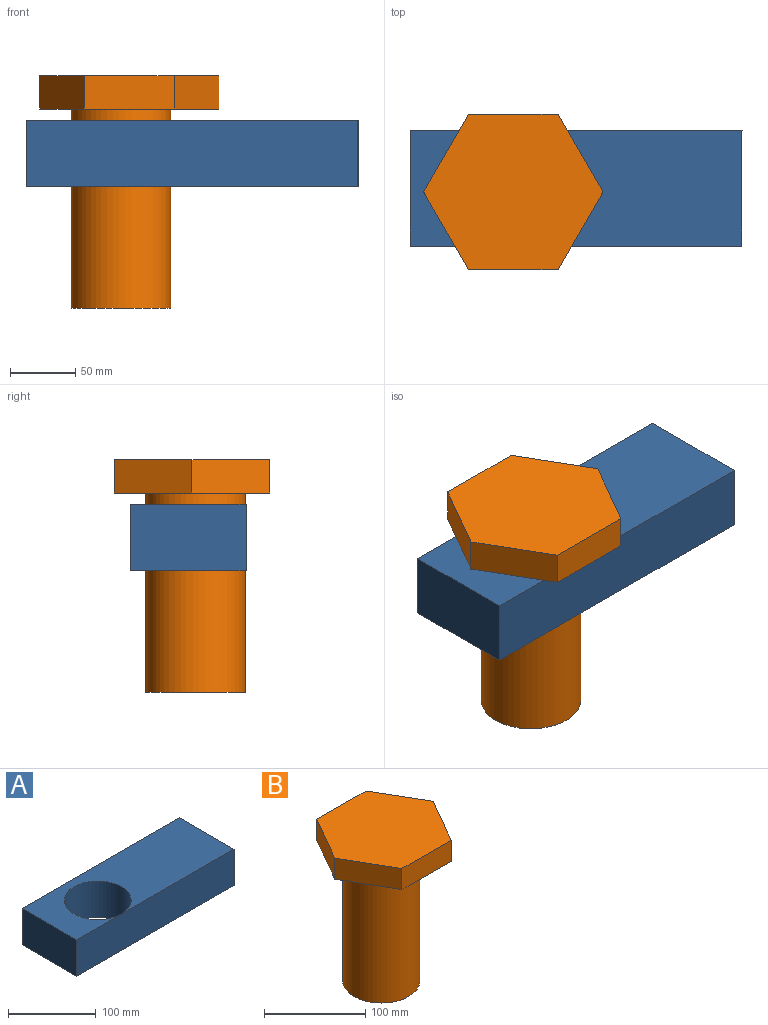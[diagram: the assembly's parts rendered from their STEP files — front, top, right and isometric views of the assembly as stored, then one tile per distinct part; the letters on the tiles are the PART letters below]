
ASSEMBLY  parts=2 mates=1
PART A: 7 faces, bbox 254x88.4x50.8 mm
  f0: plane 254x50.8mm, normal (0,1,0), area 12903.2mm2, adj f1,f4,f5,f6
  f1: plane 88.43x50.8mm, normal (-1,0,0), area 4492.5mm2, adj f0,f2,f5,f6
  f2: plane 254x50.8mm, normal (0,-1,0), area 12903.2mm2, adj f1,f4,f5,f6
  f3: cylinder r=38.1mm len=76.2mm, axis (0,0,-1), area 12161mm2, adj f5,f6
  f4: plane 88.43x50.8mm, normal (1,0,0), area 4492.5mm2, adj f0,f2,f5,f6
  f5: plane 254x88.43mm, normal (0,0,1), area 17901.9mm2, adj f0,f1,f2,f3,f4
  f6: plane 254x88.43mm, normal (0,0,-1), area 17901.9mm2, adj f0,f1,f2,f3,f4
PART B: 10 faces, bbox 137.1x118.8x177.8 mm
  f0: cylinder r=38.1mm len=152.4mm, axis (0,0,-1), area 36482.9mm2, adj f1,f9
  f1: plane 76.2x76.2mm, normal (0,0,-1), area 4560.4mm2, adj f0
  f2: plane 59.38x34.28mm, normal (-0.87,-0.5,0), area 1741.6mm2, adj f3,f7,f8,f9
  f3: plane 68.57x25.4mm, normal (0,-1,0), area 1741.6mm2, adj f2,f4,f8,f9
  f4: plane 59.38x34.28mm, normal (0.87,-0.5,0), area 1741.6mm2, adj f3,f5,f8,f9
  f5: plane 59.38x34.28mm, normal (0.87,0.5,0), area 1741.6mm2, adj f4,f6,f8,f9
  f6: plane 68.57x25.4mm, normal (0,1,0), area 1741.6mm2, adj f5,f7,f8,f9
  f7: plane 59.38x34.28mm, normal (-0.87,0.5,0), area 1741.6mm2, adj f2,f6,f8,f9
  f8: plane 137.14x118.76mm, normal (0,0,1), area 12215mm2, adj f2,f3,f4,f5,f6,f7
  f9: plane 137.14x118.76mm, normal (0,0,-1), area 7654.6mm2, adj f0,f2,f3,f4,f5,f6,f7
PLACE A t=(103.94,-119.18,418.31)mm
PLACE B t=(50.14,-141.3,325.43)mm
MATE cylindrical B.f0 <-> A.f3  axis (0,0,-1) through (-55.45,-119.18,401.63)mm
